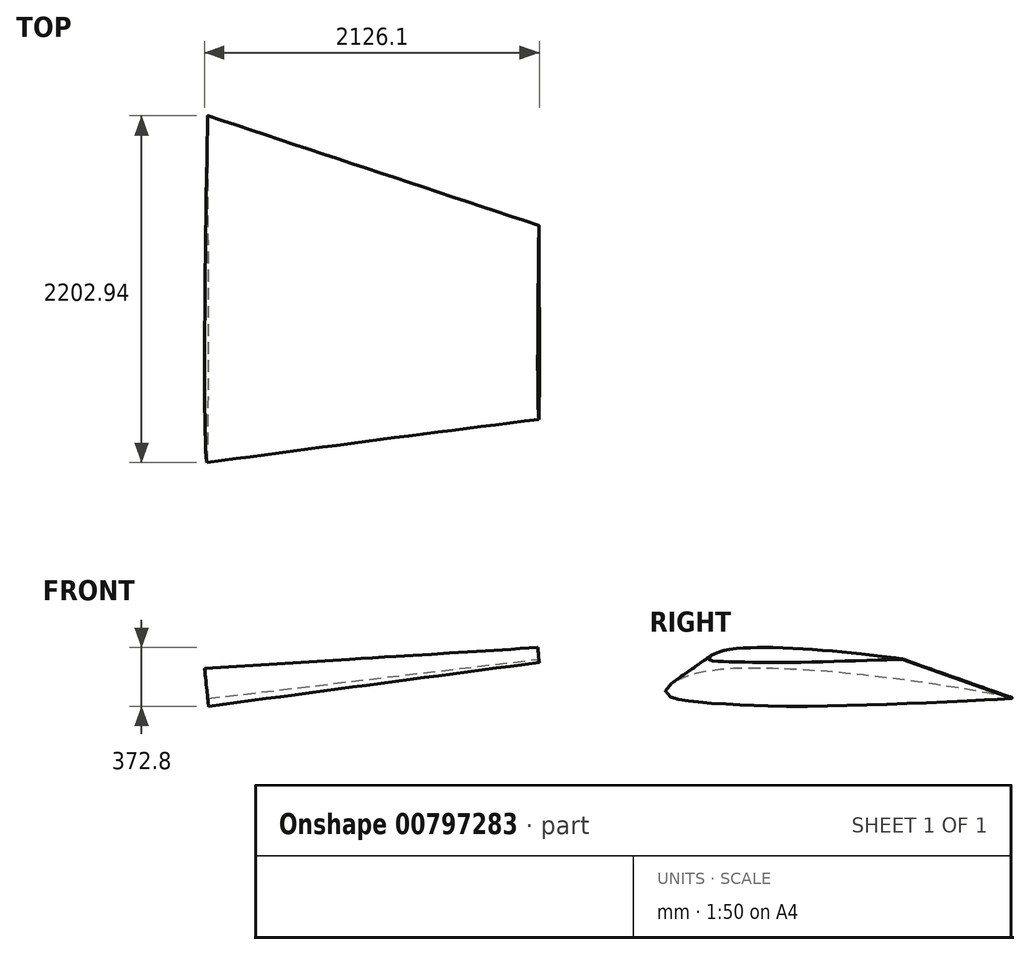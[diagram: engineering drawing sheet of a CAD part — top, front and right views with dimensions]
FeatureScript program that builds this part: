
annotation { "Feature Type Name" : "Feature", "Feature Type Description" : "" }
export const myFeature = defineFeature(function(context is Context, id is Id, definition is map)
    precondition{}
    {
        {
            var Q0;
            Q0=qCreatedBy(makeId("Right.planeOp"),FACE);
            cPlane(context, id + "F0", {"entities" : qUnion([Q0]), "cplaneType" : CPlaneType.OFFSET, "offset" : 787.4 * mm, "width" : 150 * mm, "height" : 150 * mm});
        }
        {
            var Q0;
            Q0=qCreatedBy(makeId("Front.planeOp"),FACE);
            var sketch = newSketch(context, id + "F1", { "sketchPlane" : qUnion([Q0])});
            skLineSegment(sketch, "E0", {"start": v(0, 0) * mm, "end": v(1110.2, 0) * mm});
            skSolve(sketch);
        }
        {
            var Q0;
            Q0=qCreatedBy(id+"F0.planeOp",FACE);
            var sketch = newSketch(context, id + "F2", { "sketchPlane" : qUnion([Q0])});
            skLineSegment(sketch, "E1", {"start": v(0, 0) * mm, "end": v(0, -110.48) * mm});
            skSolve(sketch);
        }
        {
            var Q0;
            Q0=qCreatedBy(id+"F0.planeOp",FACE);
            var sketch = newSketch(context, id + "F3", { "sketchPlane" : qUnion([Q0])});
            skLineSegment(sketch, "E2", {"start": v(245.37, 0) * mm, "end": v(-294.93, 0) * mm});
            skSolve(sketch);
        }
        {
            var Q0;
            Q0=qCreatedBy(id+"F0.planeOp",FACE);
            var Q1;
            Q1=sQuery(id+"F3.wireOp",EDGE,"E2");
            cPlane(context, id + "F4", {"entities" : qUnion([Q0, Q1]), "cplaneType" : CPlaneType.LINE_ANGLE, "offset" : 25 * mm, "angle" : 6 * degree, "width" : 150 * mm, "height" : 150 * mm});
        }
        {
            var Q0;
            Q0=qCreatedBy(id+"F4.planeOp",FACE);
            cPlane(context, id + "F5", {"entities" : qUnion([Q0]), "cplaneType" : CPlaneType.OFFSET, "offset" : 2021.84 * mm, "oppositeDirection" : true, "width" : 150 * mm, "height" : 150 * mm});
        }
        {
            var Q0;
            Q0=qCreatedBy(id+"F4.planeOp",FACE);
            cPlane(context, id + "F6", {"entities" : qUnion([Q0]), "cplaneType" : CPlaneType.OFFSET, "offset" : 4140.2 * mm, "oppositeDirection" : true, "width" : 150 * mm, "height" : 150 * mm});
        }
        {
            var Q0;
            Q0=qCreatedBy(id+"F5.planeOp",FACE);
            var sketch = newSketch(context, id + "F7", { "sketchPlane" : qUnion([Q0])});
            skLineSegment(sketch, "E3.0", {"start": v(0, -82.3) * mm, "end": v(0, -192.18) * mm, "construction": true});
            skLineSegment(sketch, "E4", {"start": v(1614.89, -82.3) * mm, "end": v(-1991.61, -82.3) * mm, "construction": true});
            skLineSegment(sketch, "E5.bottom", {"start": v(0, -82.3) * mm, "end": v(-1107.7, -82.3) * mm, "construction": true});
            skLineSegment(sketch, "E5.top", {"start": v(0, -32.3) * mm, "end": v(-1107.7, -32.3) * mm, "construction": true});
            skLineSegment(sketch, "E5.left", {"start": v(0, -82.3) * mm, "end": v(0, -32.3) * mm, "construction": true});
            skLineSegment(sketch, "E5.right", {"start": v(-1107.7, -82.3) * mm, "end": v(-1107.7, -32.3) * mm, "construction": true});
            skLineSegment(sketch, "E6", {"start": v(-1107.7, -82.3) * mm, "end": v(-1107.7, -206.6) * mm, "construction": true});
            skLineSegment(sketch, "E7.bottom", {"start": v(-1107.7, -82.3) * mm, "end": v(-1307.69, -82.3) * mm, "construction": true});
            skLineSegment(sketch, "E7.left", {"start": v(-1107.7, -82.3) * mm, "end": v(-1107.69, -101.1) * mm, "construction": true});
            skLineSegment(sketch, "E8", {"start": v(-1674.89, -110.73) * mm, "end": v(1055.74, -64.39) * mm, "construction": true});
            skLineSegment(sketch, "E9", {"start": v(0, -82.3) * mm, "end": v(525.7, -73.38) * mm, "construction": true});
            skLineSegment(sketch, "E10", {"start": v(525.7, -73.38) * mm, "end": v(398.72, -75.54) * mm, "construction": true});
            skLineSegment(sketch, "E11", {"start": v(398.72, -75.54) * mm, "end": v(398.3, -50.14) * mm, "construction": true});
            skLineSegment(sketch, "E12", {"start": v(525.7, -73.38) * mm, "end": v(398.3, -50.14) * mm, "construction": true});
            skCircle(sketch, "E13", {"center": v(511.71, -70.83) * mm, "radius": 14.22 * mm, "construction": true});
            skLineSegment(sketch, "E14", {"start": v(529.4, -290.9) * mm, "end": v(522.51, 114.58) * mm, "construction": true});
            skLineSegment(sketch, "E15.0", {"start": v(501.74, -282.35) * mm, "end": v(494.75, 129.39) * mm, "construction": true});
            skLineSegment(sketch, "E16.0", {"start": v(474.3, -287.14) * mm, "end": v(467.57, 109.61) * mm, "construction": true});
            skLineSegment(sketch, "E17.0", {"start": v(419.4, -294.94) * mm, "end": v(412.4, 116.94) * mm, "construction": true});
            skLineSegment(sketch, "E18.0", {"start": v(364.24, -287.45) * mm, "end": v(357.5, 109.4) * mm, "construction": true});
            skLineSegment(sketch, "E19.0", {"start": v(199.3, -296.5) * mm, "end": v(192.42, 108.98) * mm, "construction": true});
            skLineSegment(sketch, "E20.0", {"start": v(89.28, -298.36) * mm, "end": v(82.4, 107.11) * mm, "construction": true});
            skLineSegment(sketch, "E21.0", {"start": v(-20.75, -300.23) * mm, "end": v(-27.64, 105.24) * mm, "construction": true});
            skLineSegment(sketch, "E22.0", {"start": v(-130.78, -302.1) * mm, "end": v(-137.66, 103.38) * mm, "construction": true});
            skLineSegment(sketch, "E23.0", {"start": v(-350.84, -305.83) * mm, "end": v(-357.72, 99.64) * mm, "construction": true});
            skLineSegment(sketch, "E24.0", {"start": v(-570.9, -309.57) * mm, "end": v(-577.79, 95.9) * mm, "construction": true});
            skLineSegment(sketch, "E25.0", {"start": v(-790.96, -313.3) * mm, "end": v(-797.85, 92.17) * mm, "construction": true});
            skLineSegment(sketch, "E26.0", {"start": v(-1011.02, -317.04) * mm, "end": v(-1017.9, 88.44) * mm, "construction": true});
            skLineSegment(sketch, "E27.0", {"start": v(-1231.08, -320.77) * mm, "end": v(-1237.96, 84.7) * mm, "construction": true});
            skLineSegment(sketch, "E28.0", {"start": v(-1451.14, -324.5) * mm, "end": v(-1458.02, 80.97) * mm, "construction": true});
            skLineSegment(sketch, "E29.0", {"start": v(-1561.16, -326.38) * mm, "end": v(-1568.04, 79.1) * mm, "construction": true});
            skLineSegment(sketch, "E30.0", {"start": v(-1671.2, -328.24) * mm, "end": v(-1678.08, 77.23) * mm, "construction": true});
            skLineSegment(sketch, "E31", {"start": v(498.2, -73.85) * mm, "end": v(497.38, -25.6) * mm, "construction": true});
            skLineSegment(sketch, "E32", {"start": v(470.7, -74.32) * mm, "end": v(469.55, -7.02) * mm, "construction": true});
            skLineSegment(sketch, "E33", {"start": v(195.61, -78.99) * mm, "end": v(193.1, 69.07) * mm, "construction": true});
            skLineSegment(sketch, "E34", {"start": v(85.59, -80.85) * mm, "end": v(82.9, 77.36) * mm, "construction": true});
            skLineSegment(sketch, "E35", {"start": v(-24.45, -82.72) * mm, "end": v(-27.2, 79.3) * mm, "construction": true});
            skLineSegment(sketch, "E36", {"start": v(-134.47, -84.59) * mm, "end": v(-137.23, 77.95) * mm, "construction": true});
            skLineSegment(sketch, "E37", {"start": v(-354.53, -88.32) * mm, "end": v(-357.18, 67.86) * mm, "construction": true});
            skLineSegment(sketch, "E38", {"start": v(-574.6, -92.06) * mm, "end": v(-577.04, 51.68) * mm, "construction": true});
            skLineSegment(sketch, "E39", {"start": v(-794.66, -95.8) * mm, "end": v(-796.76, 28.4) * mm, "construction": true});
            skLineSegment(sketch, "E40", {"start": v(-1014.71, -99.53) * mm, "end": v(-1016.41, 0.54) * mm, "construction": true});
            skLineSegment(sketch, "E41", {"start": v(-1234.77, -103.26) * mm, "end": v(-1236, -31.13) * mm, "construction": true});
            skLineSegment(sketch, "E42", {"start": v(-1454.83, -107) * mm, "end": v(-1455.5, -67.63) * mm, "construction": true});
            skLineSegment(sketch, "E43.0", {"start": v(309.34, -294.63) * mm, "end": v(302.46, 110.85) * mm, "construction": true});
            skLineSegment(sketch, "E44", {"start": v(305.65, -77.12) * mm, "end": v(303.47, 50.88) * mm, "construction": true});
            skLineSegment(sketch, "E45", {"start": v(-1564.85, -108.86) * mm, "end": v(-1565.22, -87.28) * mm, "construction": true});
            skLineSegment(sketch, "E46", {"start": v(-1674.89, -110.73) * mm, "end": v(-1674.94, -107.94) * mm, "construction": true});
            skLineSegment(sketch, "E47", {"start": v(498.2, -73.85) * mm, "end": v(498.68, -102.04) * mm, "construction": true});
            skLineSegment(sketch, "E48", {"start": v(470.7, -74.32) * mm, "end": v(471.34, -112.66) * mm, "construction": true});
            skLineSegment(sketch, "E49", {"start": v(415.67, -75.25) * mm, "end": v(414.08, 18.72) * mm, "construction": true});
            skLineSegment(sketch, "E50", {"start": v(360.66, -76.18) * mm, "end": v(358.74, 37.08) * mm, "construction": true});
            skLineSegment(sketch, "E51", {"start": v(415.67, -75.25) * mm, "end": v(416.5, -124.26) * mm, "construction": true});
            skLineSegment(sketch, "E52", {"start": v(360.66, -76.18) * mm, "end": v(361.59, -131.04) * mm, "construction": true});
            skLineSegment(sketch, "E53", {"start": v(305.65, -77.12) * mm, "end": v(306.67, -137.3) * mm, "construction": true});
            skLineSegment(sketch, "E54", {"start": v(195.61, -78.99) * mm, "end": v(196.75, -146.04) * mm, "construction": true});
            skLineSegment(sketch, "E55", {"start": v(85.59, -80.85) * mm, "end": v(86.8, -152.47) * mm, "construction": true});
            skLineSegment(sketch, "E56", {"start": v(-24.45, -82.72) * mm, "end": v(-23.2, -156.62) * mm, "construction": true});
            skLineSegment(sketch, "E57", {"start": v(-134.47, -84.59) * mm, "end": v(-133.17, -161.03) * mm, "construction": true});
            skLineSegment(sketch, "E58", {"start": v(-354.53, -88.32) * mm, "end": v(-353.27, -162.73) * mm, "construction": true});
            skLineSegment(sketch, "E59", {"start": v(-574.6, -92.06) * mm, "end": v(-573.45, -159.87) * mm, "construction": true});
            skLineSegment(sketch, "E60", {"start": v(-794.66, -95.8) * mm, "end": v(-793.68, -153.44) * mm, "construction": true});
            skLineSegment(sketch, "E61", {"start": v(-1014.71, -99.53) * mm, "end": v(-1013.93, -145.5) * mm, "construction": true});
            skLineSegment(sketch, "E62", {"start": v(-1234.77, -103.26) * mm, "end": v(-1234.21, -136.28) * mm, "construction": true});
            skLineSegment(sketch, "E63", {"start": v(-1454.83, -107) * mm, "end": v(-1454.52, -125.53) * mm, "construction": true});
            skLineSegment(sketch, "E64", {"start": v(-1564.85, -108.86) * mm, "end": v(-1564.67, -119.78) * mm, "construction": true});
            skLineSegment(sketch, "E65", {"start": v(-1674.89, -110.73) * mm, "end": v(-1674.85, -113.27) * mm, "construction": true});
            skFitSpline(sketch, "E66", {"points": [v(-1674.94, -107.94) * mm, v(-1565.22, -87.28) * mm, v(-1455.5, -67.63) * mm, v(-1236, -31.13) * mm, v(-1016.41, 0.54) * mm, v(-796.76, 28.4) * mm, v(-577.04, 51.68) * mm, v(-357.18, 67.86) * mm, v(-137.23, 77.95) * mm, v(-27.2, 79.3) * mm, v(82.9, 77.36) * mm, v(193.1, 69.07) * mm, v(303.47, 50.88) * mm, v(358.74, 37.08) * mm, v(414.08, 18.72) * mm, v(469.55, -7.02) * mm, v(497.38, -25.6) * mm, v(525.7, -73.38) * mm, v(498.68, -102.04) * mm, v(471.34, -112.66) * mm, v(416.5, -124.26) * mm, v(361.59, -131.04) * mm, v(306.67, -137.3) * mm, v(196.75, -146.04) * mm, v(86.8, -152.47) * mm, v(-23.2, -156.62) * mm, v(-133.17, -161.03) * mm, v(-353.27, -162.73) * mm, v(-573.45, -159.87) * mm, v(-793.68, -153.44) * mm, v(-1013.93, -145.5) * mm, v(-1234.21, -136.28) * mm, v(-1454.52, -125.53) * mm, v(-1564.67, -119.78) * mm, v(-1674.85, -113.27) * mm], "startDerivative": vector(3987.05, 757.1) * mm, "endDerivative": vector(-4027.3, 243.87) * mm});
            skArc(sketch, "E67", {"start": v(-1674.94, -107.94) * mm, "mid": v(-1677.14, -110.65) * mm, "end": v(-1674.85, -113.27) * mm});
            skSolve(sketch);
        }
        {
            var Q0;
            Q0=qCreatedBy(id+"F6.planeOp",FACE);
            var sketch = newSketch(context, id + "F8", { "sketchPlane" : qUnion([Q0])});
            skLineSegment(sketch, "E68.bottom", {"start": v(0, -82.3) * mm, "end": v(-755.14, -82.3) * mm, "construction": true});
            skLineSegment(sketch, "E68.top", {"start": v(0, 81.09) * mm, "end": v(-755.14, 81.09) * mm, "construction": true});
            skLineSegment(sketch, "E68.left", {"start": v(0, -82.3) * mm, "end": v(0, 81.09) * mm, "construction": true});
            skLineSegment(sketch, "E68.right", {"start": v(-755.14, -82.3) * mm, "end": v(-755.14, 81.09) * mm, "construction": true});
            skLineSegment(sketch, "E69", {"start": v(-755.14, -82.3) * mm, "end": v(-755.14, -84.09) * mm, "construction": true});
            skLineSegment(sketch, "E70", {"start": v(-6344.55, -97.26) * mm, "end": v(753.8, -80.53) * mm, "construction": true});
            skLineSegment(sketch, "E71", {"start": v(0, -82.3) * mm, "end": v(251.46, -81.71) * mm, "construction": true});
            skLineSegment(sketch, "E72", {"start": v(251.46, -81.71) * mm, "end": v(124.46, -82.01) * mm, "construction": true});
            skLineSegment(sketch, "E73", {"start": v(124.46, -82.01) * mm, "end": v(124.4, -56.61) * mm, "construction": true});
            skLineSegment(sketch, "E74", {"start": v(124.4, -56.61) * mm, "end": v(251.46, -81.71) * mm, "construction": true});
            skCircle(sketch, "E75", {"center": v(247.6, -80.95) * mm, "radius": 3.93 * mm, "construction": true});
            skLineSegment(sketch, "E76", {"start": v(252.85, -672.62) * mm, "end": v(250.18, 461.17) * mm, "construction": true});
            skLineSegment(sketch, "E77.0", {"start": v(237.47, -672.65) * mm, "end": v(234.8, 461.13) * mm, "construction": true});
            skLineSegment(sketch, "E78.0", {"start": v(222.1, -672.7) * mm, "end": v(219.42, 461.1) * mm, "construction": true});
            skLineSegment(sketch, "E79.0", {"start": v(191.33, -672.76) * mm, "end": v(188.66, 461.03) * mm, "construction": true});
            skLineSegment(sketch, "E80.0", {"start": v(160.57, -672.84) * mm, "end": v(157.9, 460.95) * mm, "construction": true});
            skLineSegment(sketch, "E81.0", {"start": v(129.81, -672.9) * mm, "end": v(127.14, 460.88) * mm, "construction": true});
            skLineSegment(sketch, "E82.0", {"start": v(68.3, -673.05) * mm, "end": v(65.62, 460.74) * mm, "construction": true});
            skLineSegment(sketch, "E83.0", {"start": v(6.77, -673.2) * mm, "end": v(4.1, 460.6) * mm, "construction": true});
            skLineSegment(sketch, "E84.0", {"start": v(-54.74, -673.34) * mm, "end": v(-57.4, 460.45) * mm, "construction": true});
            skLineSegment(sketch, "E85.0", {"start": v(-116.26, -673.49) * mm, "end": v(-118.93, 460.3) * mm, "construction": true});
            skLineSegment(sketch, "E86.0", {"start": v(-239.3, -673.78) * mm, "end": v(-241.97, 460.01) * mm, "construction": true});
            skLineSegment(sketch, "E87.0", {"start": v(-362.34, -674.07) * mm, "end": v(-365, 459.72) * mm, "construction": true});
            skLineSegment(sketch, "E88.0", {"start": v(-485.38, -674.36) * mm, "end": v(-488.05, 459.43) * mm, "construction": true});
            skLineSegment(sketch, "E89.0", {"start": v(-608.4, -674.65) * mm, "end": v(-611.08, 459.14) * mm, "construction": true});
            skLineSegment(sketch, "E90.0", {"start": v(-731.45, -674.94) * mm, "end": v(-734.12, 458.85) * mm, "construction": true});
            skLineSegment(sketch, "E91.0", {"start": v(-854.48, -675.23) * mm, "end": v(-857.16, 458.56) * mm, "construction": true});
            skLineSegment(sketch, "E92.0", {"start": v(-916, -675.37) * mm, "end": v(-918.68, 458.42) * mm, "construction": true});
            skLineSegment(sketch, "E93.0", {"start": v(-977.52, -675.52) * mm, "end": v(-980.2, 458.27) * mm, "construction": true});
            skLineSegment(sketch, "E94", {"start": v(236.08, -81.75) * mm, "end": v(236.03, -62.45) * mm, "construction": true});
            skLineSegment(sketch, "E95", {"start": v(220.7, -81.79) * mm, "end": v(220.63, -54.1) * mm, "construction": true});
            skLineSegment(sketch, "E96", {"start": v(189.94, -81.86) * mm, "end": v(189.85, -41.98) * mm, "construction": true});
            skLineSegment(sketch, "E97", {"start": v(159.18, -81.93) * mm, "end": v(159.06, -32.4) * mm, "construction": true});
            skLineSegment(sketch, "E98", {"start": v(128.42, -82) * mm, "end": v(128.29, -25.61) * mm, "construction": true});
            skLineSegment(sketch, "E99", {"start": v(66.9, -82.15) * mm, "end": v(66.75, -16.87) * mm, "construction": true});
            skLineSegment(sketch, "E100", {"start": v(5.38, -82.3) * mm, "end": v(5.22, -12.44) * mm, "construction": true});
            skLineSegment(sketch, "E101", {"start": v(-56.13, -82.44) * mm, "end": v(-56.3, -11.07) * mm, "construction": true});
            skLineSegment(sketch, "E102", {"start": v(-117.65, -82.58) * mm, "end": v(-117.82, -10.7) * mm, "construction": true});
            skLineSegment(sketch, "E103", {"start": v(-240.69, -82.87) * mm, "end": v(-240.85, -14.04) * mm, "construction": true});
            skLineSegment(sketch, "E104", {"start": v(-363.73, -83.16) * mm, "end": v(-363.88, -20.17) * mm, "construction": true});
            skLineSegment(sketch, "E105", {"start": v(-486.77, -83.45) * mm, "end": v(-486.9, -28.84) * mm, "construction": true});
            skLineSegment(sketch, "E106", {"start": v(-609.8, -83.74) * mm, "end": v(-609.9, -39.8) * mm, "construction": true});
            skLineSegment(sketch, "E107", {"start": v(-732.84, -84.03) * mm, "end": v(-732.91, -52.28) * mm, "construction": true});
            skLineSegment(sketch, "E108", {"start": v(-855.88, -84.32) * mm, "end": v(-855.92, -67.05) * mm, "construction": true});
            skLineSegment(sketch, "E109", {"start": v(-917.4, -84.47) * mm, "end": v(-917.42, -75.07) * mm, "construction": true});
            skLineSegment(sketch, "E110", {"start": v(-978.92, -84.61) * mm, "end": v(-978.92, -83.6) * mm, "construction": true});
            skLineSegment(sketch, "E111", {"start": v(236.08, -81.75) * mm, "end": v(236.1, -92.42) * mm, "construction": true});
            skLineSegment(sketch, "E112", {"start": v(220.7, -81.79) * mm, "end": v(220.73, -95.76) * mm, "construction": true});
            skLineSegment(sketch, "E113", {"start": v(189.94, -81.86) * mm, "end": v(189.98, -98.62) * mm, "construction": true});
            skLineSegment(sketch, "E114", {"start": v(159.18, -81.93) * mm, "end": v(159.22, -100.22) * mm, "construction": true});
            skLineSegment(sketch, "E115", {"start": v(128.42, -82) * mm, "end": v(128.47, -101.3) * mm, "construction": true});
            skLineSegment(sketch, "E116", {"start": v(66.9, -82.15) * mm, "end": v(66.95, -102.98) * mm, "construction": true});
            skLineSegment(sketch, "E117", {"start": v(5.38, -82.3) * mm, "end": v(5.43, -104.4) * mm, "construction": true});
            skLineSegment(sketch, "E118", {"start": v(-56.13, -82.44) * mm, "end": v(-56.08, -105.3) * mm, "construction": true});
            skLineSegment(sketch, "E119", {"start": v(-117.65, -82.58) * mm, "end": v(-117.6, -105.44) * mm, "construction": true});
            skLineSegment(sketch, "E120", {"start": v(-240.69, -82.87) * mm, "end": v(-240.64, -105.73) * mm, "construction": true});
            skLineSegment(sketch, "E121", {"start": v(-363.73, -83.16) * mm, "end": v(-363.68, -104) * mm, "construction": true});
            skLineSegment(sketch, "E122", {"start": v(-486.77, -83.45) * mm, "end": v(-486.73, -100.98) * mm, "construction": true});
            skLineSegment(sketch, "E123", {"start": v(-609.8, -83.74) * mm, "end": v(-609.77, -97.71) * mm, "construction": true});
            skLineSegment(sketch, "E124", {"start": v(-732.84, -84.03) * mm, "end": v(-732.81, -93.94) * mm, "construction": true});
            skLineSegment(sketch, "E125", {"start": v(-855.88, -84.32) * mm, "end": v(-855.86, -89.91) * mm, "construction": true});
            skLineSegment(sketch, "E126", {"start": v(-917.4, -84.47) * mm, "end": v(-917.39, -88.03) * mm, "construction": true});
            skLineSegment(sketch, "E127", {"start": v(-978.92, -84.61) * mm, "end": v(-978.91, -85.63) * mm, "construction": true});
            skFitSpline(sketch, "E128", {"points": [v(-978.92, -83.6) * mm, v(-917.42, -75.07) * mm, v(-732.91, -52.28) * mm, v(-609.9, -39.8) * mm, v(-486.9, -28.84) * mm, v(-363.88, -20.17) * mm, v(-240.85, -14.04) * mm, v(-117.82, -10.7) * mm, v(-56.3, -11.07) * mm, v(5.22, -12.44) * mm, v(66.75, -16.87) * mm, v(128.29, -25.61) * mm, v(159.06, -32.4) * mm, v(189.85, -41.98) * mm, v(220.63, -54.1) * mm, v(236.03, -62.45) * mm, v(251.46, -81.71) * mm, v(236.1, -92.42) * mm, v(220.73, -95.76) * mm, v(189.98, -98.62) * mm, v(159.22, -100.22) * mm, v(128.47, -101.3) * mm, v(66.95, -102.98) * mm, v(5.43, -104.4) * mm, v(-56.08, -105.3) * mm, v(-117.6, -105.44) * mm, v(-240.64, -105.73) * mm, v(-363.68, -104) * mm, v(-486.73, -100.98) * mm, v(-609.77, -97.71) * mm, v(-732.81, -93.94) * mm, v(-855.86, -89.91) * mm, v(-917.39, -88.03) * mm, v(-978.91, -85.63) * mm], "startDerivative": vector(1776.94, 254.67) * mm, "endDerivative": vector(-2195.24, 90.15) * mm});
            skArc(sketch, "E129", {"start": v(-978.92, -83.6) * mm, "mid": v(-979.8, -84.62) * mm, "end": v(-978.91, -85.63) * mm});
            skSolve(sketch);
        }
        {
            var Q0;
            Q0 = qSketchRegion(id + "F7", true);
            var Q1;
            Q1 = qSketchRegion(id + "F8", true);
            var Q2;
            Q2 = qConstructionFilter(qBodyType(qCreatedBy(id + "F7" ,EDGE), BodyType.WIRE), ConstructionObject.NO);
            var Q3;
            Q3 = qConstructionFilter(qBodyType(qCreatedBy(id + "F8" ,EDGE), BodyType.WIRE), ConstructionObject.NO);
            loft(context, id + "F9", {"sheetProfilesArray" : [{ "sheetProfileEntities" : qUnion([Q0]) }, { "sheetProfileEntities" : qUnion([Q1]) }], "wireProfilesArray" : [{ "wireProfileEntities" : qUnion([Q2]) }, { "wireProfileEntities" : qUnion([Q3]) }]});
        }
    });
